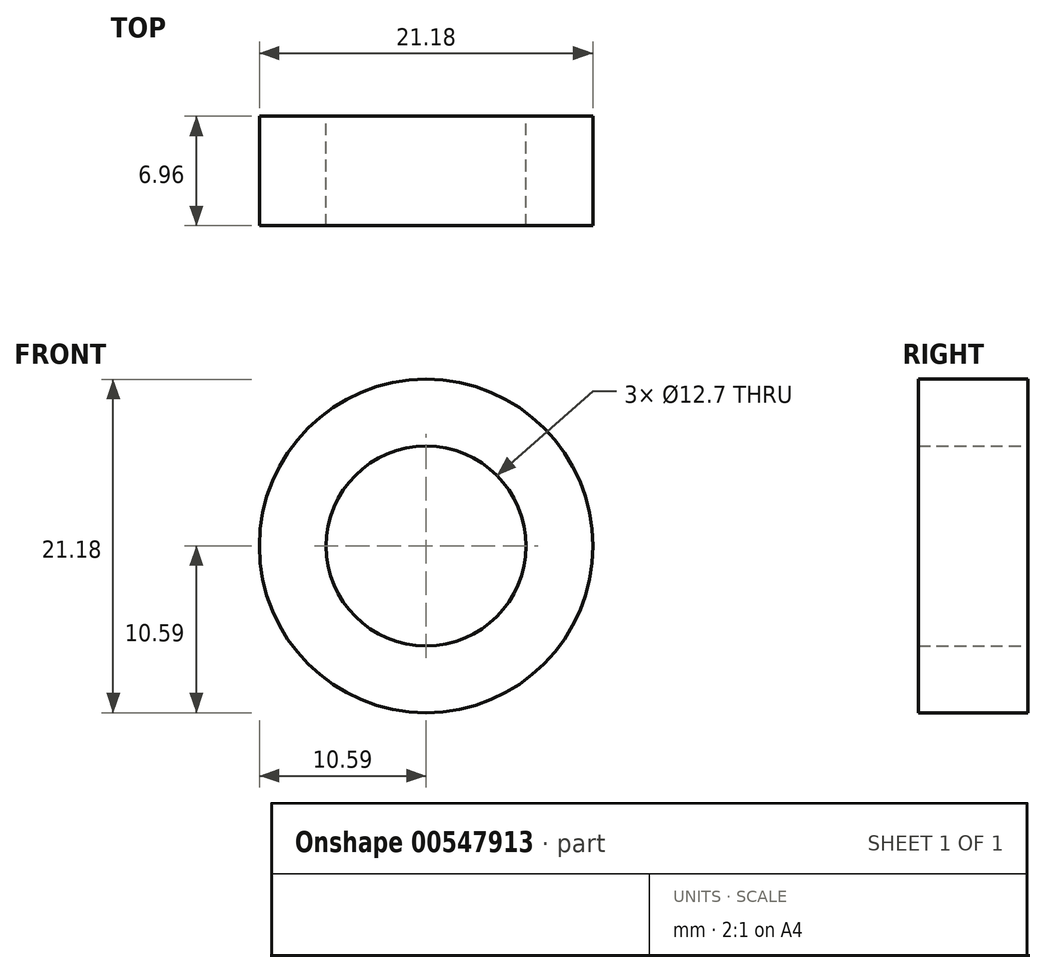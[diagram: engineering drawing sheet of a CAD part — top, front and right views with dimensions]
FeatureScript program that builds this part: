
annotation { "Feature Type Name" : "Feature", "Feature Type Description" : "" }
export const myFeature = defineFeature(function(context is Context, id is Id, definition is map)
    precondition{}
    {
        {
            var Q0;
            Q0=qCreatedBy(makeId("Front.planeOp"),FACE);
            var sketch = newSketch(context, id + "F0", { "sketchPlane" : qUnion([Q0])});
            skCircle(sketch, "E0", {"center": v(0, 0) * mm, "radius": 10.6 * mm});
            skCircle(sketch, "E1", {"center": v(0, 0) * mm, "radius": 6.35 * mm});
            skSolve(sketch);
        }
        {
            var Q0;
            Q0=makeQuery(id+"F0.imprint","IMPRINT",FACE,{"disambiguationData":[TD([[makeQuery(id+"F0.imprint","IMPRINT",EDGE,{"derivedFrom":sQuery(id+"F0.wireOp",EDGE,"E0")}),1.0]])]});
            extrude(context, id + "F1", {"entities" : qUnion([Q0]), "depth" : 6.96 * mm, "offsetDistance" : 25.4 * mm});
        }
        {
            var Q0;
            Q0=makeQuery(id+"F1.opExtrude","SWEPT_BODY",BODY,{"disambiguationData":[OSD([sQuery(id+"F0.wireOp",EDGE,"E0"),sQuery(id+"F0.wireOp",EDGE,"E1")])]});
            transform(context, id + "F2", {"entities" : qUnion([Q0]), "transformType" : TransformType.TRANSLATION_3D, "dx" : 0 * mm, "dy" : -3.48 * mm, "dz" : 0 * mm, "makeCopy" : false});
        }
    });
